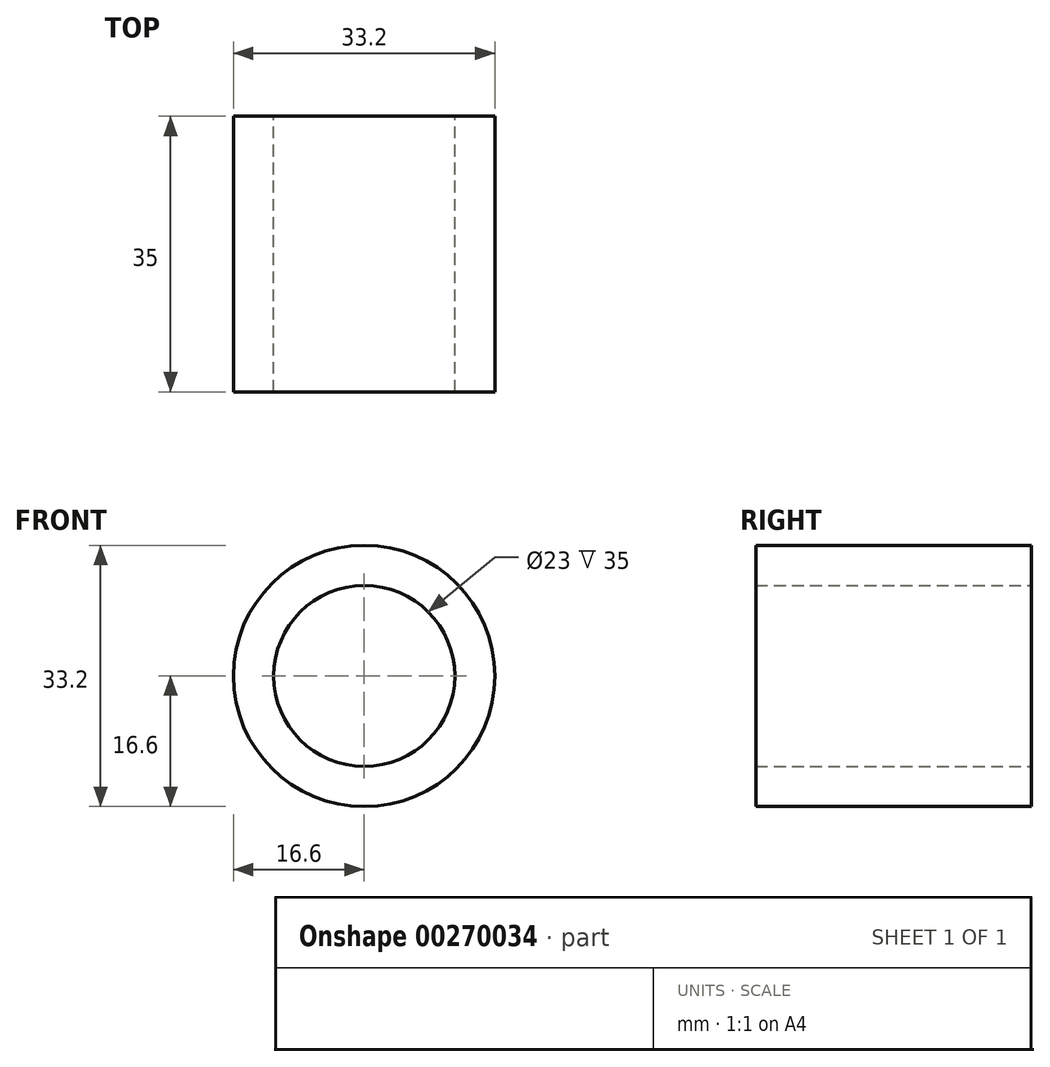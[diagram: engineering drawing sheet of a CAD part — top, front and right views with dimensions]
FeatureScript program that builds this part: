
annotation { "Feature Type Name" : "Feature", "Feature Type Description" : "" }
export const myFeature = defineFeature(function(context is Context, id is Id, definition is map)
    precondition{}
    {
        {
            var Q0;
            Q0=qCreatedBy(makeId("Front.planeOp"),FACE);
            var sketch = newSketch(context, id + "F0", { "sketchPlane" : qUnion([Q0])});
            skCircle(sketch, "E0", {"center": v(0, 0) * mm, "radius": 25 * mm});
            skCircle(sketch, "E1", {"center": v(0, 0) * mm, "radius": 5 * mm});
            skCircle(sketch, "E2", {"center": v(0, 0) * mm, "radius": 11.5 * mm});
            skSolve(sketch);
        }
        {
            var Q0;
            Q0=makeQuery(id+"F0.imprint","IMPRINT",FACE,{"disambiguationData":[TD([[makeQuery(id+"F0.imprint","IMPRINT",EDGE,{"derivedFrom":sQuery(id+"F0.wireOp",EDGE,"E0")}),1.0]])]});
            extrude(context, id + "F1", {"entities" : qUnion([Q0]), "depth" : 17.5 * mm, "offsetDistance" : 25 * mm, "hasSecondDirection" : true, "secondDirectionOppositeDirection" : true, "secondDirectionDepth" : 17.5 * mm});
        }
        {
            var Q0;
            Q0=makeQuery(id+"F0.imprint","IMPRINT",FACE,{"disambiguationData":[TD([[makeQuery(id+"F0.imprint","IMPRINT",EDGE,{"derivedFrom":sQuery(id+"F0.wireOp",EDGE,"E1")}),-1.0]])]});
            extrude(context, id + "F2", {"entities" : qUnion([Q0]), "operationType" : NewBodyOperationType.ADD, "depth" : 6 * mm, "offsetDistance" : 25 * mm});
        }
        {
            var Q0;
            Q0=makeQuery(id+"F0.imprint","IMPRINT",FACE,{"disambiguationData":[TD([[makeQuery(id+"F0.imprint","IMPRINT",EDGE,{"derivedFrom":sQuery(id+"F0.wireOp",EDGE,"E1")}),-1.0]])]});
            extrude(context, id + "F3", {"entities" : qUnion([Q0]), "operationType" : NewBodyOperationType.ADD, "oppositeDirection" : true, "depth" : 6 * mm, "offsetDistance" : 25 * mm});
        }
        {
            var Q0;
            Q0=makeQuery(id+"F1.opExtrude","CAP_EDGE",EDGE,{"disambiguationData":[OSD([sQuery(id+"F0.wireOp",EDGE,"E0")])],"isStart":false});
            var Q1;
            Q1=makeQuery(id+"F1.opExtrude","CAP_EDGE",EDGE,{"disambiguationData":[OSD([sQuery(id+"F0.wireOp",EDGE,"E0")])],"isStart":true});
            fillet(context, id + "F4", {"entities" : qUnion([Q0, Q1]), "radius" : 8.4 * mm, "tangentPropagation" : true, "allowEdgeOverflow" : false});
        }
        {
            var Q0;
            Q0=qCreatedBy(makeId("Top.planeOp"),FACE);
            var sketch = newSketch(context, id + "F5", { "sketchPlane" : qUnion([Q0])});
            skLineSegment(sketch, "E3.0", {"start": v(11.5, 0) * mm, "end": v(-11.5, 0) * mm});
            skLineSegment(sketch, "E4", {"start": v(25, 9.53) * mm, "end": v(25, -9.53) * mm});
            skLineSegment(sketch, "E5", {"start": v(-25, -9.53) * mm, "end": v(-25, 9.53) * mm});
            skSolve(sketch);
        }
        {
            var Q0;
            Q0=makeQuery(id+"F1.opExtrude","CAP_FACE",FACE,{"disambiguationData":[OSD([sQuery(id+"F0.wireOp",EDGE,"E0"),sQuery(id+"F0.wireOp",EDGE,"E2")])],"isStart":true});
            extrude(context, id + "F6", {"entities" : qUnion([Q0]), "operationType" : NewBodyOperationType.INTERSECT, "oppositeDirection" : true, "depth" : 83.1 * mm, "offsetDistance" : 25 * mm});
        }
    });
